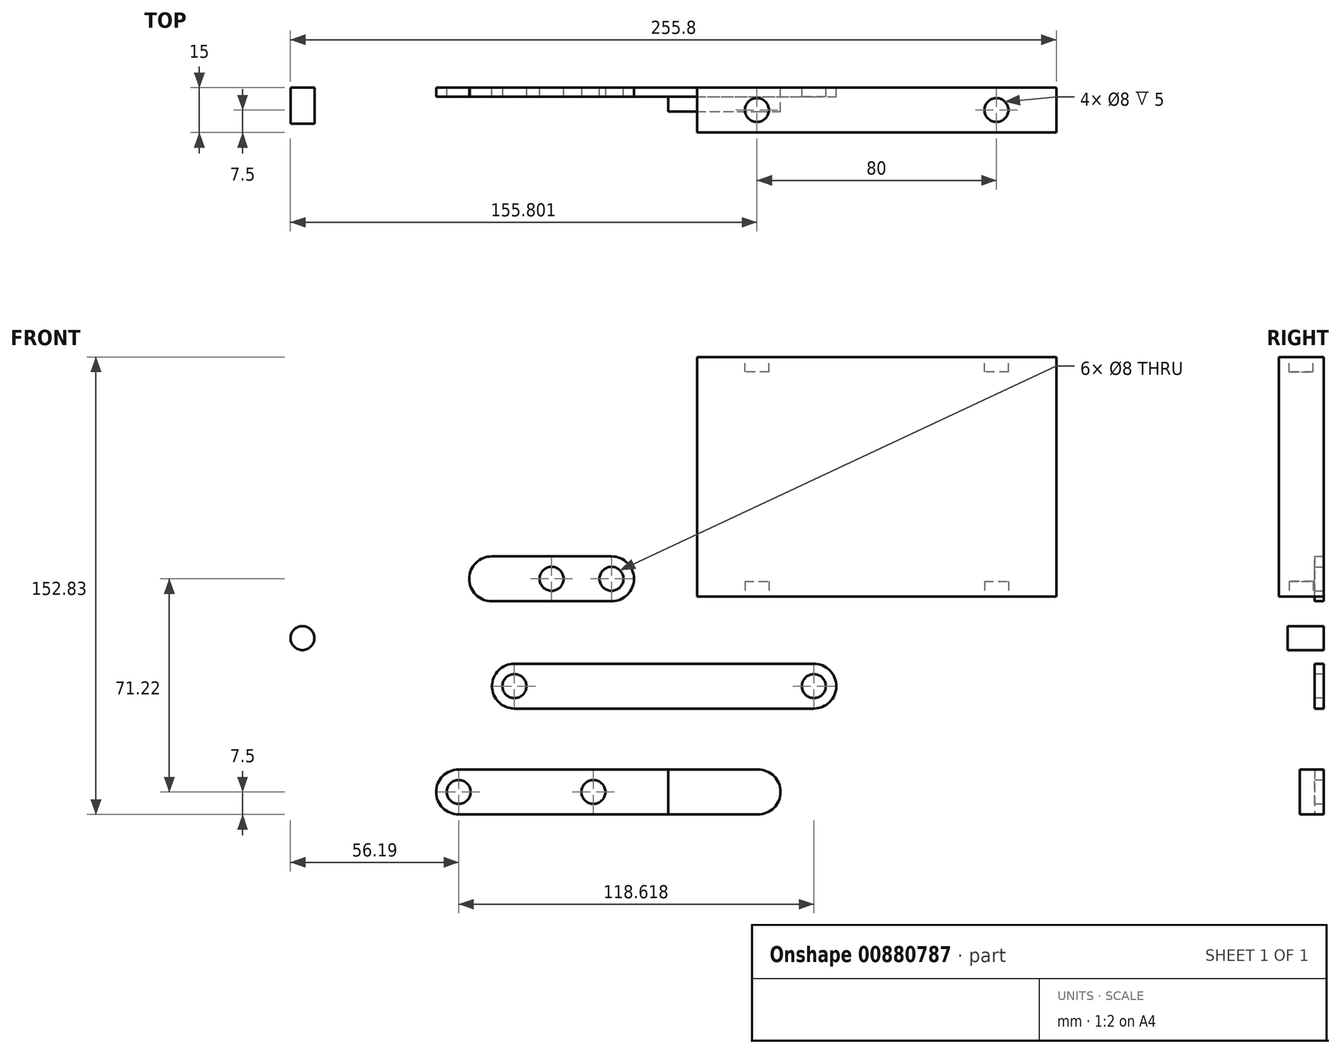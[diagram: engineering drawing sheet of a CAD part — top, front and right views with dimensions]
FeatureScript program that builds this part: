
annotation { "Feature Type Name" : "Feature", "Feature Type Description" : "" }
export const myFeature = defineFeature(function(context is Context, id is Id, definition is map)
    precondition{}
    {
        {
            var Q0;
            Q0=qCreatedBy(makeId("Front.planeOp"),FACE);
            var sketch = newSketch(context, id + "F0", { "sketchPlane" : qUnion([Q0])});
            skLineSegment(sketch, "E0.bottom", {"start": v(-46.94, 6.58) * mm, "end": v(53.06, 6.58) * mm});
            skLineSegment(sketch, "E0.top", {"start": v(-46.94, -8.42) * mm, "end": v(53.06, -8.42) * mm});
            skArc(sketch, "E1", {"start": v(-46.94, 6.58) * mm, "mid": v(-54.44, -0.92) * mm, "end": v(-46.94, -8.42) * mm});
            skArc(sketch, "E2", {"start": v(53.06, -8.42) * mm, "mid": v(60.56, -0.92) * mm, "end": v(53.06, 6.58) * mm});
            skSolve(sketch);
        }
        {
            var Q0;
            Q0 = qSketchRegion(id + "F0", true);
            extrude(context, id + "F1", {"entities" : qUnion([Q0]), "depth" : 3 * mm, "offsetDistance" : 25 * mm});
        }
        {
            var Q0;
            Q0=qCreatedBy(makeId("Front.planeOp"),FACE);
            var sketch = newSketch(context, id + "F2", { "sketchPlane" : qUnion([Q0])});
            skLineSegment(sketch, "E3.bottom", {"start": v(-65.56, -28.8) * mm, "end": v(34.44, -28.8) * mm});
            skLineSegment(sketch, "E3.top", {"start": v(-65.56, -43.8) * mm, "end": v(34.44, -43.8) * mm});
            skArc(sketch, "E4", {"start": v(-65.56, -28.8) * mm, "mid": v(-73.06, -36.3) * mm, "end": v(-65.56, -43.8) * mm});
            skArc(sketch, "E5", {"start": v(34.44, -43.8) * mm, "mid": v(41.94, -36.3) * mm, "end": v(34.44, -28.8) * mm});
            skSolve(sketch);
        }
        {
            var Q0;
            Q0 = qSketchRegion(id + "F2", true);
            extrude(context, id + "F3", {"entities" : qUnion([Q0]), "depth" : 3 * mm, "offsetDistance" : 25 * mm});
        }
        {
            var Q0;
            Q0=makeQuery(id+"F3.opExtrude","CAP_FACE",FACE,{"disambiguationData":[OSD([sQuery(id+"F2.wireOp",EDGE,"E3.bottom"),sQuery(id+"F2.wireOp",EDGE,"E3.top"),sQuery(id+"F2.wireOp",EDGE,"E4"),sQuery(id+"F2.wireOp",EDGE,"E5")])],"isStart":false});
            var sketch = newSketch(context, id + "F4", { "sketchPlane" : qUnion([Q0])});
            skLineSegment(sketch, "E6.bottom", {"start": v(4.44, -28.8) * mm, "end": v(34.44, -28.8) * mm});
            skLineSegment(sketch, "E6.top", {"start": v(4.44, -43.8) * mm, "end": v(34.44, -43.8) * mm});
            skLineSegment(sketch, "E6.left", {"start": v(4.44, -28.8) * mm, "end": v(4.44, -43.8) * mm});
            skArc(sketch, "E7", {"start": v(34.44, -43.8) * mm, "mid": v(41.94, -36.3) * mm, "end": v(34.44, -28.8) * mm});
            skSolve(sketch);
        }
        {
            var Q0;
            Q0 = qSketchRegion(id + "F4", true);
            extrude(context, id + "F5", {"entities" : qUnion([Q0]), "operationType" : NewBodyOperationType.ADD, "depth" : 5 * mm, "offsetDistance" : 25 * mm});
        }
        {
            var Q0;
            Q0=makeQuery(id+"F1.opExtrude","CAP_FACE",FACE,{"disambiguationData":[OSD([sQuery(id+"F0.wireOp",EDGE,"E0.bottom"),sQuery(id+"F0.wireOp",EDGE,"E0.top"),sQuery(id+"F0.wireOp",EDGE,"E1"),sQuery(id+"F0.wireOp",EDGE,"E2")])],"isStart":false});
            var sketch = newSketch(context, id + "F6", { "sketchPlane" : qUnion([Q0])});
            skCircle(sketch, "E8", {"center": v(53.06, -0.92) * mm, "radius": 4 * mm});
            skCircle(sketch, "E9", {"center": v(-46.94, -0.92) * mm, "radius": 4 * mm});
            skSolve(sketch);
        }
        {
            var Q0;
            Q0 = qSketchRegion(id + "F6", true);
            extrude(context, id + "F7", {"entities" : qUnion([Q0]), "operationType" : NewBodyOperationType.REMOVE, "oppositeDirection" : true, "depth" : 25 * mm, "offsetDistance" : 25 * mm});
        }
        {
            var Q0;
            Q0=makeQuery(id+"F5.opExtrude","CAP_FACE",FACE,{"disambiguationData":[OSD([sQuery(id+"F4.wireOp",EDGE,"E6.bottom"),sQuery(id+"F4.wireOp",EDGE,"E6.top"),sQuery(id+"F4.wireOp",EDGE,"E6.left"),sQuery(id+"F4.wireOp",EDGE,"E7")])],"isStart":false});
            var sketch = newSketch(context, id + "F8", { "sketchPlane" : qUnion([Q0])});
            skCircle(sketch, "E10", {"center": v(-65.56, -36.3) * mm, "radius": 4 * mm});
            skCircle(sketch, "E11", {"center": v(-20.56, -36.3) * mm, "radius": 4 * mm});
            skSolve(sketch);
        }
        {
            var Q0;
            Q0 = qSketchRegion(id + "F8", true);
            extrude(context, id + "F9", {"entities" : qUnion([Q0]), "operationType" : NewBodyOperationType.REMOVE, "oppositeDirection" : true, "depth" : 25 * mm, "offsetDistance" : 25 * mm});
        }
        {
            var Q0;
            Q0=qCreatedBy(makeId("Front.planeOp"),FACE);
            var sketch = newSketch(context, id + "F10", { "sketchPlane" : qUnion([Q0])});
            skLineSegment(sketch, "E12.bottom", {"start": v(-54.52, 42.43) * mm, "end": v(-14.52, 42.43) * mm});
            skLineSegment(sketch, "E12.top", {"start": v(-54.52, 27.43) * mm, "end": v(-14.52, 27.43) * mm});
            skArc(sketch, "E13", {"start": v(-54.52, 42.43) * mm, "mid": v(-62.02, 34.93) * mm, "end": v(-54.52, 27.43) * mm});
            skArc(sketch, "E14", {"start": v(-14.52, 27.43) * mm, "mid": v(-7.02, 34.93) * mm, "end": v(-14.52, 42.43) * mm});
            skCircle(sketch, "E15", {"center": v(-14.52, 34.93) * mm, "radius": 4 * mm});
            skCircle(sketch, "E16", {"center": v(-34.52, 34.93) * mm, "radius": 4 * mm});
            skSolve(sketch);
        }
        {
            var Q0;
            Q0 = qSketchRegion(id + "F10", true);
            extrude(context, id + "F11", {"entities" : qUnion([Q0]), "depth" : 3 * mm, "offsetDistance" : 25 * mm});
        }
        {
            var Q0;
            Q0=qCreatedBy(makeId("Front.planeOp"),FACE);
            var sketch = newSketch(context, id + "F12", { "sketchPlane" : qUnion([Q0])});
            skLineSegment(sketch, "E17.bottom", {"start": v(14.05, 109.04) * mm, "end": v(134.05, 109.04) * mm});
            skLineSegment(sketch, "E17.top", {"start": v(14.05, 29.04) * mm, "end": v(134.05, 29.04) * mm});
            skLineSegment(sketch, "E17.left", {"start": v(14.05, 109.04) * mm, "end": v(14.05, 29.04) * mm});
            skLineSegment(sketch, "E17.right", {"start": v(134.05, 109.04) * mm, "end": v(134.05, 29.04) * mm});
            skSolve(sketch);
        }
        {
            var Q0;
            Q0 = qSketchRegion(id + "F12", true);
            extrude(context, id + "F13", {"entities" : qUnion([Q0]), "depth" : 15 * mm, "offsetDistance" : 25 * mm});
        }
        {
            var Q0;
            Q0=makeQuery(id+"F13.opExtrude","SWEPT_FACE",FACE,{"disambiguationData":[OSD([sQuery(id+"F12.wireOp",EDGE,"E17.top")])]});
            var sketch = newSketch(context, id + "F14", { "sketchPlane" : qUnion([Q0])});
            skCircle(sketch, "E18", {"center": v(34.05, 7.5) * mm, "radius": 4 * mm});
            skCircle(sketch, "E19", {"center": v(114.05, 7.5) * mm, "radius": 4 * mm});
            skSolve(sketch);
        }
        {
            var Q0;
            Q0 = qSketchRegion(id + "F14", true);
            extrude(context, id + "F15", {"entities" : qUnion([Q0]), "operationType" : NewBodyOperationType.REMOVE, "oppositeDirection" : true, "depth" : 5 * mm, "offsetDistance" : 25 * mm});
        }
        {
            var Q0;
            Q0=makeQuery(id+"F13.opExtrude","SWEPT_FACE",FACE,{"disambiguationData":[OSD([sQuery(id+"F12.wireOp",EDGE,"E17.bottom")])]});
            var sketch = newSketch(context, id + "F16", { "sketchPlane" : qUnion([Q0])});
            skCircle(sketch, "E20", {"center": v(34.05, -7.5) * mm, "radius": 4 * mm});
            skCircle(sketch, "E21", {"center": v(114.05, -7.5) * mm, "radius": 4 * mm});
            skSolve(sketch);
        }
        {
            var Q0;
            Q0 = qSketchRegion(id + "F16", true);
            extrude(context, id + "F17", {"entities" : qUnion([Q0]), "operationType" : NewBodyOperationType.REMOVE, "oppositeDirection" : true, "depth" : 5 * mm, "offsetDistance" : 25 * mm});
        }
        {
            var Q0;
            Q0=qCreatedBy(makeId("Front.planeOp"),FACE);
            var sketch = newSketch(context, id + "F18", { "sketchPlane" : qUnion([Q0])});
            skCircle(sketch, "E22", {"center": v(-117.75, 15.13) * mm, "radius": 4 * mm});
            skSolve(sketch);
        }
        {
            var Q0;
            Q0 = qSketchRegion(id + "F18", true);
            extrude(context, id + "F19", {"entities" : qUnion([Q0]), "depth" : 12 * mm, "offsetDistance" : 25 * mm});
        }
    });
